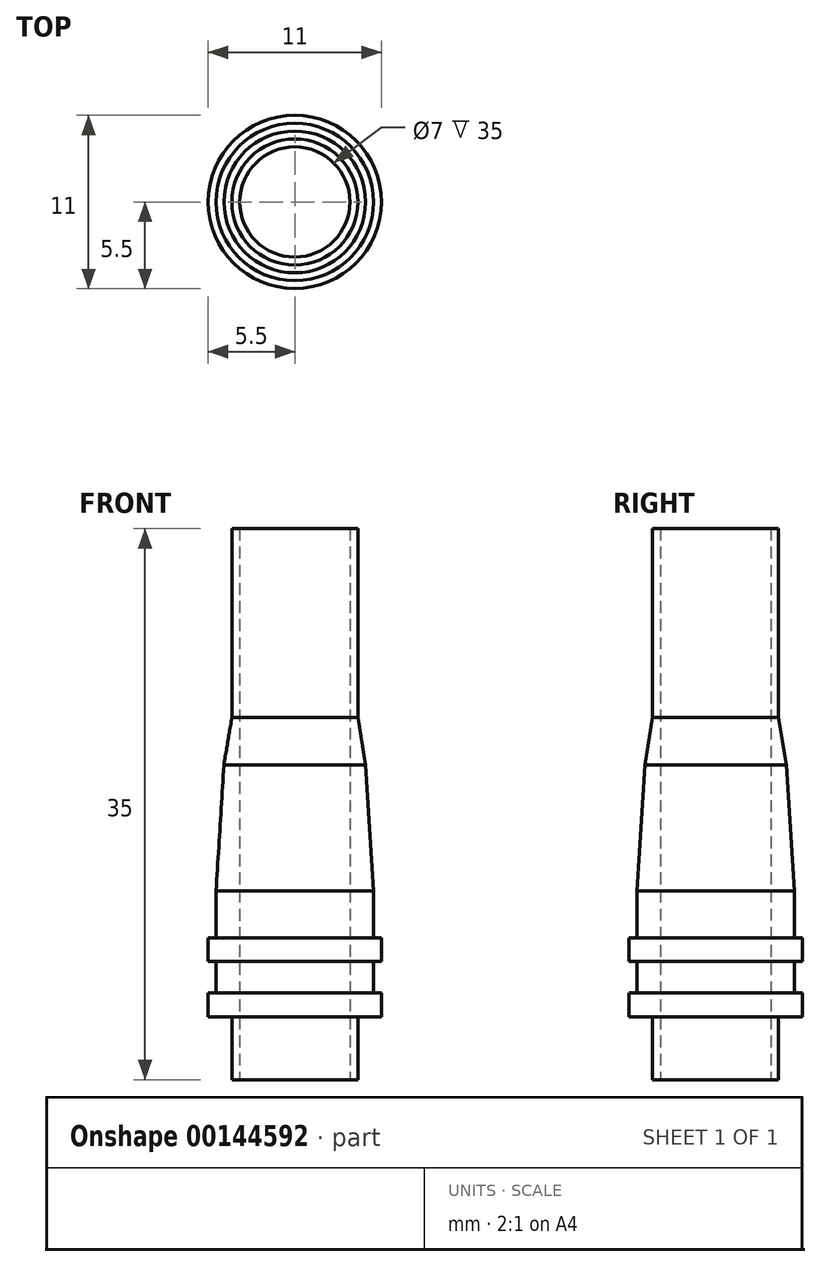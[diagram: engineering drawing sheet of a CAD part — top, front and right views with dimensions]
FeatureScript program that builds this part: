
annotation { "Feature Type Name" : "Feature", "Feature Type Description" : "" }
export const myFeature = defineFeature(function(context is Context, id is Id, definition is map)
    precondition{}
    {
        {
            var Q0;
            Q0=qCreatedBy(makeId("Front.planeOp"),FACE);
            var sketch = newSketch(context, id + "F0", { "sketchPlane" : qUnion([Q0])});
            skLineSegment(sketch, "E0", {"start": v(0, 0) * mm, "end": v(0, 35) * mm});
            skLineSegment(sketch, "E1", {"start": v(0, 35) * mm, "end": v(-4, 35) * mm});
            skLineSegment(sketch, "E2", {"start": v(-4.5, 20) * mm, "end": v(-5, 12) * mm});
            skLineSegment(sketch, "E3", {"start": v(-5, 12) * mm, "end": v(-5, 9) * mm});
            skLineSegment(sketch, "E4", {"start": v(-5, 9) * mm, "end": v(-5.5, 9) * mm});
            skLineSegment(sketch, "E5", {"start": v(-5.5, 9) * mm, "end": v(-5.5, 7.5) * mm});
            skLineSegment(sketch, "E6", {"start": v(-5.5, 7.5) * mm, "end": v(-5, 7.5) * mm});
            skLineSegment(sketch, "E7", {"start": v(-5, 7.5) * mm, "end": v(-5, 5.5) * mm});
            skLineSegment(sketch, "E8", {"start": v(-5, 5.5) * mm, "end": v(-5.5, 5.5) * mm});
            skLineSegment(sketch, "E9", {"start": v(-5.5, 5.5) * mm, "end": v(-5.5, 4) * mm});
            skLineSegment(sketch, "E10", {"start": v(-5.5, 4) * mm, "end": v(-4, 4) * mm});
            skLineSegment(sketch, "E11", {"start": v(-4, 4) * mm, "end": v(-4, 0) * mm});
            skLineSegment(sketch, "E12", {"start": v(-4, 0) * mm, "end": v(0, 0) * mm});
            skLineSegment(sketch, "E13", {"start": v(-4, 23) * mm, "end": v(-4, 35) * mm});
            skLineSegment(sketch, "E14", {"start": v(-4.5, 20) * mm, "end": v(-4, 23) * mm});
            skSolve(sketch);
        }
        {
            var Q0;
            Q0=makeQuery(id+"F0.imprint","IMPRINT",FACE,{"disambiguationData":[TD([[makeQuery(id+"F0.imprint","IMPRINT",EDGE,{"derivedFrom":sQuery(id+"F0.wireOp",EDGE,"E0")}),1.0]])]});
            var Q1;
            Q1=sQuery(id+"F0.wireOp",EDGE,"E0");
            revolve(context, id + "F1", {"entities" : qUnion([Q0]), "axis" : qUnion([Q1]), "revolveType" : RevolveType.FULL});
        }
        {
            var Q0;
            Q0=makeQuery(id+"F1.opRevolve","SWEPT_FACE",FACE,{"disambiguationData":[OSD([sQuery(id+"F0.wireOp",EDGE,"E12")])]});
            var sketch = newSketch(context, id + "F2", { "sketchPlane" : qUnion([Q0])});
            skCircle(sketch, "E15", {"center": v(0, 0) * mm, "radius": 3.5 * mm});
            skSolve(sketch);
        }
        {
            var Q0;
            Q0=sQuery(id+"F2.wireOp",VERTEX,"E15.center");
            var Q1;
            Q1=makeQuery(id+"F1.opRevolve","SWEPT_BODY",BODY,{"disambiguationData":[OSD([sQuery(id+"F0.wireOp",EDGE,"E0"),sQuery(id+"F0.wireOp",EDGE,"E1"),sQuery(id+"F0.wireOp",EDGE,"xdqxE60K-c3G7-wjra-WEiu-yTtULkGZajOb"),sQuery(id+"F0.wireOp",EDGE,"UmnBso5e-Hba4-rJuE-Obe2-RMrWLW22lOX2"),sQuery(id+"F0.wireOp",EDGE,"E2"),sQuery(id+"F0.wireOp",EDGE,"E3"),sQuery(id+"F0.wireOp",EDGE,"E4"),sQuery(id+"F0.wireOp",EDGE,"E5"),sQuery(id+"F0.wireOp",EDGE,"E6"),sQuery(id+"F0.wireOp",EDGE,"E7"),sQuery(id+"F0.wireOp",EDGE,"E8"),sQuery(id+"F0.wireOp",EDGE,"E9"),sQuery(id+"F0.wireOp",EDGE,"E10"),sQuery(id+"F0.wireOp",EDGE,"E11"),sQuery(id+"F0.wireOp",EDGE,"E12")])]});
            hole(context, id + "F3", {"style" : HoleStyle.SIMPLE, "endStyle" : HoleEndStyle.THROUGH, "holeDiameter" : 7 * mm, "locations" : qUnion([Q0]), "scope" : qUnion([Q1]), "isTappedThrough" : true});
        }
    });
